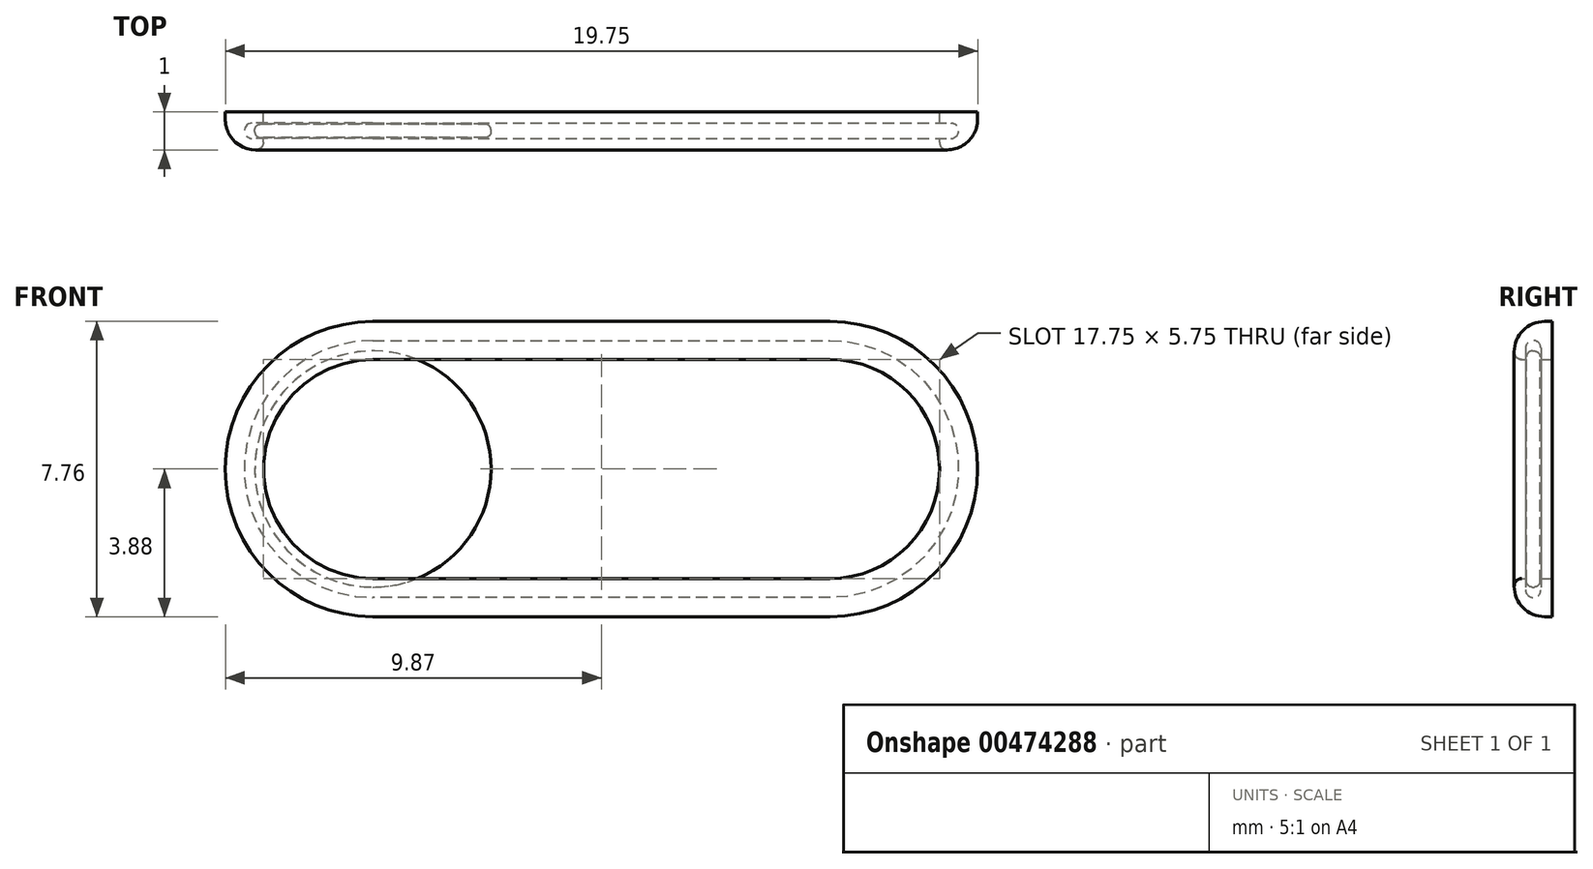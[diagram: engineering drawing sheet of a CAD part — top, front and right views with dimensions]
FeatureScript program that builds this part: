
annotation { "Feature Type Name" : "Feature", "Feature Type Description" : "" }
export const myFeature = defineFeature(function(context is Context, id is Id, definition is map)
    precondition{}
    {
        {
            var Q0;
            Q0=qCreatedBy(makeId("Front.planeOp"),FACE);
            var sketch = newSketch(context, id + "F0", { "sketchPlane" : qUnion([Q0])});
            skLineSegment(sketch, "E0.bottom", {"start": v(-6, 2.87) * mm, "end": v(6, 2.87) * mm});
            skLineSegment(sketch, "E0.top", {"start": v(-6, -2.88) * mm, "end": v(6, -2.88) * mm});
            skPoint(sketch, "E0.middle", {"position": v(0, 0) * mm});
            skArc(sketch, "E1", {"start": v(-6, 2.87) * mm, "mid": v(-8.87, 0) * mm, "end": v(-6, -2.87) * mm});
            skArc(sketch, "E2", {"start": v(6, 2.88) * mm, "mid": v(8.88, 0) * mm, "end": v(6, -2.88) * mm});
            skLineSegment(sketch, "E3.0", {"start": v(-6, 3.87) * mm, "end": v(6, 3.87) * mm});
            skArc(sketch, "E3.1", {"start": v(-6, 3.87) * mm, "mid": v(-9.87, 0) * mm, "end": v(-6, -3.88) * mm});
            skLineSegment(sketch, "E3.2", {"start": v(-6, -3.88) * mm, "end": v(6, -3.88) * mm});
            skArc(sketch, "E3.3", {"start": v(6, 3.88) * mm, "mid": v(9.88, 0) * mm, "end": v(6, -3.88) * mm});
            skLineSegment(sketch, "E4.0", {"start": v(-6, 3.37) * mm, "end": v(6, 3.37) * mm});
            skArc(sketch, "E4.1", {"start": v(-6, 3.37) * mm, "mid": v(-9.37, 0) * mm, "end": v(-6, -3.38) * mm});
            skLineSegment(sketch, "E4.2", {"start": v(-6, -3.38) * mm, "end": v(6, -3.38) * mm});
            skArc(sketch, "E4.3", {"start": v(6, 3.38) * mm, "mid": v(9.38, 0) * mm, "end": v(6, -3.38) * mm});
            skLineSegment(sketch, "E5.0", {"start": v(-6, 2.62) * mm, "end": v(6, 2.62) * mm, "construction": true});
            skArc(sketch, "E5.1", {"start": v(-6, 2.62) * mm, "mid": v(-8.62, 0) * mm, "end": v(-6, -2.63) * mm, "construction": true});
            skLineSegment(sketch, "E5.2", {"start": v(-6, -2.63) * mm, "end": v(6, -2.63) * mm, "construction": true});
            skArc(sketch, "E5.3", {"start": v(6, 2.63) * mm, "mid": v(8.63, 0) * mm, "end": v(6, -2.63) * mm, "construction": true});
            skSolve(sketch);
        }
        {
            var Q0;
            Q0=makeQuery(id+"F0.imprint","IMPRINT",FACE,{"disambiguationData":[TD([[makeQuery(id+"F0.imprint","IMPRINT",EDGE,{"derivedFrom":sQuery(id+"F0.wireOp",EDGE,"E0.bottom")}),1.0]])]});
            var Q1;
            Q1=makeQuery(id+"F0.imprint","IMPRINT",FACE,{"disambiguationData":[TD([[makeQuery(id+"F0.imprint","IMPRINT",EDGE,{"derivedFrom":sQuery(id+"F0.wireOp",EDGE,"E3.0")}),-1.0]])]});
            extrude(context, id + "F1", {"entities" : qUnion([Q0, Q1]), "endBound" : BoundingType.SYMMETRIC, "depth" : 1 * mm});
        }
        {
            var Q0;
            Q0=makeQuery(id+"F0.imprint","IMPRINT",FACE,{"disambiguationData":[TD([[makeQuery(id+"F0.imprint","IMPRINT",EDGE,{"derivedFrom":sQuery(id+"F0.wireOp",EDGE,"E0.bottom")}),1.0]])]});
            var Q1;
            Q1=makeQuery(id+"F0.imprint","IMPRINT",FACE,{"disambiguationData":[TD([[makeQuery(id+"F0.imprint","IMPRINT",EDGE,{"derivedFrom":sQuery(id+"F0.wireOp",EDGE,"E0.bottom")}),-1.0]])]});
            extrude(context, id + "F2", {"entities" : qUnion([Q0, Q1]), "operationType" : NewBodyOperationType.REMOVE, "endBound" : BoundingType.SYMMETRIC, "oppositeDirection" : true, "depth" : .4 * mm});
        }
        {
            var Q0;
            Q0=makeQuery(id+"F2.boolean.opBoolean","COPY",EDGE,{"derivedFrom":makeQuery(id+"F2.opExtrude","CAP_EDGE",EDGE,{"disambiguationData":[OSD([sQuery(id+"F0.wireOp",EDGE,"E4.0")])],"isStart":true})});
            var Q1;
            Q1=makeQuery(id+"F2.boolean.opBoolean","COPY",EDGE,{"derivedFrom":makeQuery(id+"F2.opExtrude","CAP_EDGE",EDGE,{"disambiguationData":[OSD([sQuery(id+"F0.wireOp",EDGE,"E4.3")])],"isStart":true})});
            var Q2;
            Q2=makeQuery(id+"F2.boolean.opBoolean","COPY",EDGE,{"derivedFrom":makeQuery(id+"F2.opExtrude","CAP_EDGE",EDGE,{"disambiguationData":[OSD([sQuery(id+"F0.wireOp",EDGE,"E4.0")])],"isStart":false})});
            var Q3;
            Q3=makeQuery(id+"F2.boolean.opBoolean","COPY",EDGE,{"derivedFrom":makeQuery(id+"F2.opExtrude","CAP_EDGE",EDGE,{"disambiguationData":[OSD([sQuery(id+"F0.wireOp",EDGE,"E4.3")])],"isStart":false})});
            var Q4;
            Q4=makeQuery(id+"F2.boolean.opBoolean","COPY",EDGE,{"derivedFrom":makeQuery(id+"F2.opExtrude","CAP_EDGE",EDGE,{"disambiguationData":[OSD([sQuery(id+"F0.wireOp",EDGE,"E4.2")])],"isStart":false})});
            var Q5;
            Q5=makeQuery(id+"F2.boolean.opBoolean","COPY",EDGE,{"derivedFrom":makeQuery(id+"F2.opExtrude","CAP_EDGE",EDGE,{"disambiguationData":[OSD([sQuery(id+"F0.wireOp",EDGE,"E4.2")])],"isStart":true})});
            var Q6;
            Q6=makeQuery(id+"F2.boolean.opBoolean","COPY",EDGE,{"derivedFrom":makeQuery(id+"F2.opExtrude","CAP_EDGE",EDGE,{"disambiguationData":[OSD([sQuery(id+"F0.wireOp",EDGE,"E4.1")])],"isStart":false})});
            var Q7;
            Q7=makeQuery(id+"F2.boolean.opBoolean","COPY",EDGE,{"derivedFrom":makeQuery(id+"F2.opExtrude","CAP_EDGE",EDGE,{"disambiguationData":[OSD([sQuery(id+"F0.wireOp",EDGE,"E4.1")])],"isStart":true})});
            fillet(context, id + "F3", {"entities" : qUnion([Q0, Q1, Q2, Q3, Q4, Q5, Q6, Q7]), "radius" : .2 * mm, "tangentPropagation" : true, "allowEdgeOverflow" : false});
        }
        {
            var Q0;
            Q0=makeQuery(id+"F1.opExtrude","CAP_EDGE",EDGE,{"disambiguationData":[OSD([sQuery(id+"F0.wireOp",EDGE,"E3.1")])],"isStart":false});
            var Q1;
            Q1=makeQuery(id+"F1.opExtrude","CAP_EDGE",EDGE,{"disambiguationData":[OSD([sQuery(id+"F0.wireOp",EDGE,"E3.0")])],"isStart":false});
            var Q2;
            Q2=makeQuery(id+"F1.opExtrude","CAP_EDGE",EDGE,{"disambiguationData":[OSD([sQuery(id+"F0.wireOp",EDGE,"E3.3")])],"isStart":false});
            var Q3;
            Q3=makeQuery(id+"F1.opExtrude","CAP_EDGE",EDGE,{"disambiguationData":[OSD([sQuery(id+"F0.wireOp",EDGE,"E3.2")])],"isStart":false});
            fillet(context, id + "F4", {"entities" : qUnion([Q0, Q1, Q2, Q3]), "radius" : .8 * mm, "tangentPropagation" : true, "allowEdgeOverflow" : false});
        }
        {
            var Q0;
            Q0=makeQuery(id+"F0.imprint","IMPRINT",FACE,{"disambiguationData":[TD([[makeQuery(id+"F0.imprint","IMPRINT",EDGE,{"derivedFrom":sQuery(id+"F0.wireOp",EDGE,"E0.bottom")}),-1.0]])]});
            var sketch = newSketch(context, id + "F5", { "sketchPlane" : qUnion([Q0])});
            skCircle(sketch, "E6", {"center": v(-6, 0) * mm, "radius": 3.1 * mm});
            skSolve(sketch);
        }
        {
            var Q0;
            Q0=qSketchRegion(id+"F5",true);
            extrude(context, id + "F6", {"entities" : qUnion([Q0]), "endBound" : BoundingType.SYMMETRIC, "depth" : .35 * mm});
        }
        {
            var Q0;
            Q0=makeQuery(id+"F6.opExtrude","CAP_EDGE",EDGE,{"disambiguationData":[OSD([sQuery(id+"F5.wireOp",EDGE,"E6")])],"isStart":false});
            var Q1;
            Q1=makeQuery(id+"F6.opExtrude","CAP_EDGE",EDGE,{"disambiguationData":[OSD([sQuery(id+"F5.wireOp",EDGE,"E6")])],"isStart":true});
            fillet(context, id + "F7", {"entities" : qUnion([Q0, Q1]), "radius" : .15 * mm, "tangentPropagation" : true, "allowEdgeOverflow" : false});
        }
        {
            var Q0;
            Q0=makeQuery(id+"F1.opExtrude","CAP_EDGE",EDGE,{"disambiguationData":[OSD([sQuery(id+"F0.wireOp",EDGE,"E0.bottom")])],"isStart":false});
            var Q1;
            Q1=makeQuery(id+"F1.opExtrude","CAP_EDGE",EDGE,{"disambiguationData":[OSD([sQuery(id+"F0.wireOp",EDGE,"E1")])],"isStart":false});
            var Q2;
            Q2=makeQuery(id+"F1.opExtrude","CAP_EDGE",EDGE,{"disambiguationData":[OSD([sQuery(id+"F0.wireOp",EDGE,"E0.top")])],"isStart":false});
            var Q3;
            Q3=makeQuery(id+"F1.opExtrude","CAP_EDGE",EDGE,{"disambiguationData":[OSD([sQuery(id+"F0.wireOp",EDGE,"E2")])],"isStart":false});
            fillet(context, id + "F8", {"entities" : qUnion([Q0, Q1, Q2, Q3]), "radius" : .2 * mm, "tangentPropagation" : true, "allowEdgeOverflow" : false});
        }
    });
